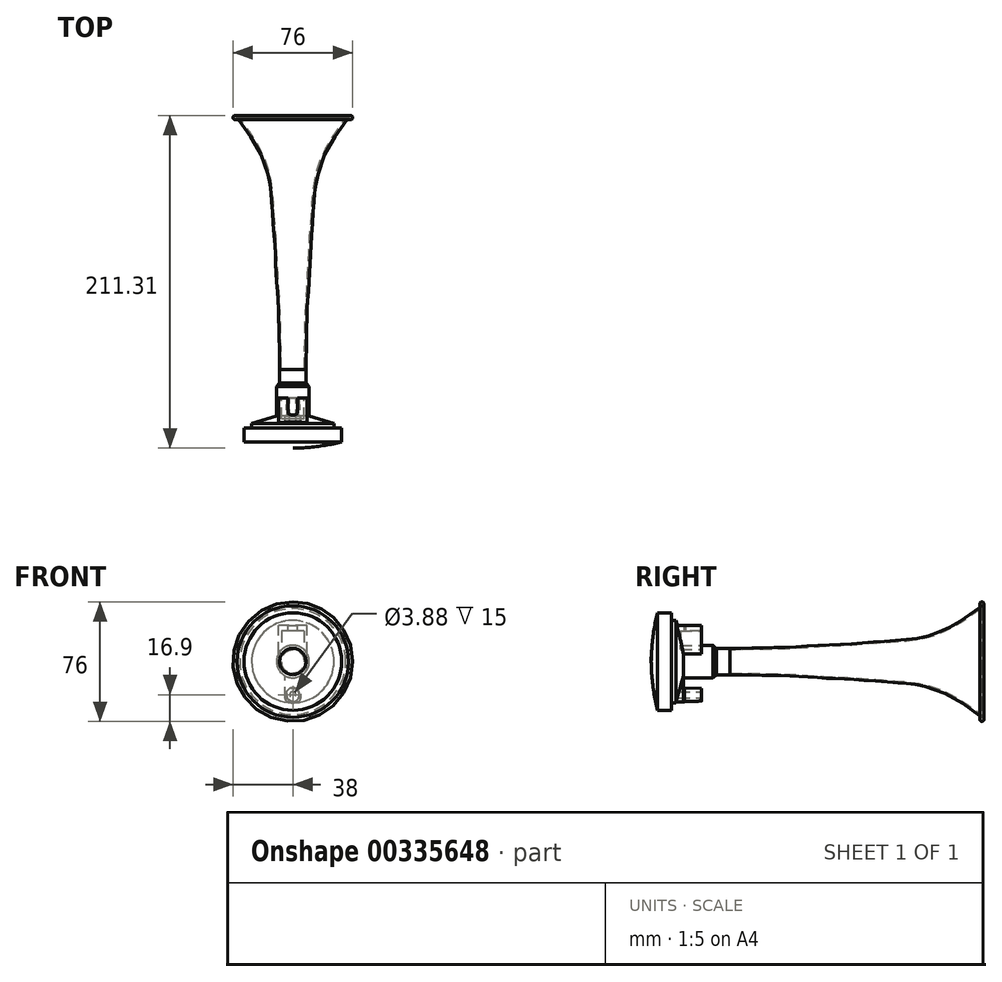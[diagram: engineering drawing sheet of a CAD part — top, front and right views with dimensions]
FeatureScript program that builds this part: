
annotation { "Feature Type Name" : "Feature", "Feature Type Description" : "" }
export const myFeature = defineFeature(function(context is Context, id is Id, definition is map)
    precondition{}
    {
        {
            var Q0;
            Q0=qCreatedBy(makeId("Right.planeOp"),FACE);
            var sketch = newSketch(context, id + "F0", { "sketchPlane" : qUnion([Q0])});
            skLineSegment(sketch, "E0", {"start": v(0, 0) * mm, "end": v(0, 36.7) * mm, "construction": true});
            skLineSegment(sketch, "E1", {"start": v(0, 36.7) * mm, "end": v(0, 36.7) * mm});
            skLineSegment(sketch, "E2", {"start": v(0, 38) * mm, "end": v(0, 36.7) * mm});
            skArc(sketch, "E3", {"start": v(1, 35.86) * mm, "mid": v(-0.55, 37.88) * mm, "end": v(0, 35.4) * mm});
            skPoint(sketch, "E4", {"position": v(1, 35.86) * mm});
            skPoint(sketch, "E5", {"position": v(-20, 0) * mm});
            skPoint(sketch, "E6.1.0.0", {"position": v(-40, 0) * mm});
            skPoint(sketch, "E6.2.0.0", {"position": v(-60, 0) * mm});
            skPoint(sketch, "E6.3.0.0", {"position": v(-80, 0) * mm});
            skPoint(sketch, "E6.4.0.0", {"position": v(-100, 0) * mm});
            skPoint(sketch, "E6.5.0.0", {"position": v(-120, 0) * mm});
            skPoint(sketch, "E6.6.0.0", {"position": v(-140, 0) * mm});
            skPoint(sketch, "E6.7.0.0", {"position": v(-160, 0) * mm});
            skPoint(sketch, "E6.8.0.0", {"position": v(-180, 0) * mm});
            skPoint(sketch, "E6.9.0.0", {"position": v(-200, 0) * mm});
            skPoint(sketch, "E6.10.0.0", {"position": v(-220, 0) * mm});
            skPoint(sketch, "E6.11.0.0", {"position": v(-240, 0) * mm});
            skLineSegment(sketch, "E6.direction1", {"start": v(-20, 0) * mm, "end": v(-40, 0) * mm, "construction": true});
            skLineSegment(sketch, "E7", {"start": v(-20, 0) * mm, "end": v(-20, 22) * mm, "construction": true});
            skLineSegment(sketch, "E8", {"start": v(-40, 0) * mm, "end": v(-40, 15) * mm, "construction": true});
            skLineSegment(sketch, "E9", {"start": v(-60, 0) * mm, "end": v(-60, 13) * mm, "construction": true});
            skLineSegment(sketch, "E10", {"start": v(-80, 0) * mm, "end": v(-80, 11.5) * mm, "construction": true});
            skLineSegment(sketch, "E11", {"start": v(-100, 0) * mm, "end": v(-100, 10.5) * mm, "construction": true});
            skLineSegment(sketch, "E12", {"start": v(-120, 0) * mm, "end": v(-120, 9.25) * mm, "construction": true});
            skLineSegment(sketch, "E13", {"start": v(-140, 0) * mm, "end": v(-140, 8.7) * mm, "construction": true});
            skLineSegment(sketch, "E14", {"start": v(-160, 0) * mm, "end": v(-160, 8.35) * mm, "construction": true});
            skFitSpline(sketch, "E15", {"points": [v(0, 35.4) * mm, v(-20, 22) * mm, v(-40, 15) * mm, v(-60, 13) * mm, v(-80, 11.5) * mm, v(-100, 10.5) * mm, v(-120, 9.25) * mm, v(-140, 8.7) * mm, v(-160, 8.35) * mm], "startDerivative": vector(-145.86, -108.6) * mm, "endDerivative": vector(-162.63, -2.88) * mm});
            skLineSegment(sketch, "E16", {"start": v(-160, 8.35) * mm, "end": v(-168.6, 8.35) * mm});
            skLineSegment(sketch, "E17", {"start": v(-168.6, 8.35) * mm, "end": v(-170.83, 10.35) * mm});
            skLineSegment(sketch, "E18", {"start": v(-170.83, 10.35) * mm, "end": v(-189.63, 10.35) * mm});
            skLineSegment(sketch, "E19", {"start": v(-189.63, 10.35) * mm, "end": v(-194.23, 26.15) * mm});
            skLineSegment(sketch, "E20", {"start": v(-194.23, 26.15) * mm, "end": v(-197.23, 26.15) * mm});
            skLineSegment(sketch, "E21", {"start": v(-197.23, 26.15) * mm, "end": v(-197.23, 31) * mm});
            skLineSegment(sketch, "E22", {"start": v(-197.23, 31) * mm, "end": v(-206, 31) * mm});
            skArc(sketch, "E23", {"start": v(-206, 31) * mm, "mid": v(-208.9, 15.62) * mm, "end": v(-210, 0) * mm});
            skFitSpline(sketch, "E24", {"points": [v(1, 35.86) * mm, v(0, 23.41) * mm, v(0, 0) * mm], "startDerivative": vector(-27.01, -39.8) * mm, "endDerivative": vector(0.68, -43.7) * mm});
            skFitSpline(sketch, "E25.0", {"points": [v(0.6, 34.6) * mm, v(-2.44, 32.34) * mm, v(-7.01, 28.93) * mm, v(-13.23, 24.75) * mm, v(-17.19, 22.36) * mm, v(-20.42, 20.64) * mm, v(-23.68, 19.05) * mm, v(-27.81, 17.32) * mm, v(-32.85, 15.63) * mm, v(-37.08, 14.55) * mm, v(-40.5, 13.88) * mm, v(-43.9, 13.33) * mm, v(-48.16, 12.83) * mm, v(-53.26, 12.43) * mm, v(-57.5, 12.17) * mm, v(-60.88, 11.94) * mm, v(-64.26, 11.69) * mm, v(-70.18, 11.22) * mm, v(-76.95, 10.67) * mm, v(-83.74, 10.27) * mm, v(-88.83, 10.03) * mm, v(-93.9, 9.8) * mm, v(-98.98, 9.57) * mm, v(-104.05, 9.26) * mm, v(-110.81, 8.8) * mm, v(-117.6, 8.34) * mm, v(-124.39, 8.05) * mm, v(-131.18, 7.85) * mm, v(-139.66, 7.7) * mm, v(-149.82, 7.53) * mm, v(-156.6, 7.41) * mm, v(-159.98, 7.35) * mm]});
            skArc(sketch, "E26.filletArc", {"start": v(-0.92, 33.47) * mm, "mid": v(-0.2, 34.13) * mm, "end": v(0.39, 34.91) * mm});
            skLineSegment(sketch, "E27", {"start": v(-159.98, 7.35) * mm, "end": v(-160, 0) * mm});
            skLineSegment(sketch, "E28", {"start": v(-160, 0) * mm, "end": v(-210, 0) * mm});
            skSolve(sketch);
        }
        {
            var Q0;
            {var subQ0=sQuery(id+"F0.wireOp",EDGE,"E15");Q0=makeQuery(id+"F0.imprint","IMPRINT",FACE,{"disambiguationData":[TD([[makeQuery(id+"F0.imprint","IMPRINT",EDGE,{"derivedFrom":subQ0}),1.0]])]});}
            var Q1;
            Q1=sQuery(id+"F0.wireOp",EDGE,"E28");
            revolve(context, id + "F1", {"entities" : qUnion([Q0]), "axis" : qUnion([Q1]), "revolveType" : RevolveType.FULL});
        }
        {
            var Q0;
            Q0=qCreatedBy(makeId("Front.planeOp"),FACE);
            cPlane(context, id + "F2", {"entities" : qUnion([Q0]), "cplaneType" : CPlaneType.OFFSET, "offset" : 178 * mm, "width" : 150 * mm, "height" : 150 * mm});
        }
        {
            var Q0;
            Q0=qCreatedBy(id+"F2.planeOp",FACE);
            var sketch = newSketch(context, id + "F3", { "sketchPlane" : qUnion([Q0])});
            skLineSegment(sketch, "E29", {"start": v(0, 0) * mm, "end": v(0, -25.5) * mm, "construction": true});
            skLineSegment(sketch, "E30", {"start": v(-4.9, -25.5) * mm, "end": v(4.9, -25.5) * mm});
            skPoint(sketch, "E31", {"position": v(0, -25.5) * mm});
            skLineSegment(sketch, "E32", {"start": v(-4.9, -25.5) * mm, "end": v(-4.9, 0) * mm});
            skLineSegment(sketch, "E33", {"start": v(-4.9, 0) * mm, "end": v(4.9, 0) * mm});
            skLineSegment(sketch, "E34", {"start": v(4.9, 0) * mm, "end": v(4.9, -25.5) * mm});
            skSolve(sketch);
        }
        {
            var Q0;
            Q0=makeQuery(id+"F3.imprint","IMPRINT",FACE,{"disambiguationData":[TD([[makeQuery(id+"F3.imprint","IMPRINT",EDGE,{"derivedFrom":sQuery(id+"F3.wireOp",EDGE,"E30")}),1.0]])]});
            extrude(context, id + "F4", {"entities" : qUnion([Q0]), "operationType" : NewBodyOperationType.ADD, "depth" : 25 * mm});
        }
        {
            var Q0;
            Q0=makeQuery(id+"F4.opExtrude","CAP_FACE",FACE,{"disambiguationData":[OSD([sQuery(id+"F3.wireOp",EDGE,"E30"),sQuery(id+"F3.wireOp",EDGE,"E32"),sQuery(id+"F3.wireOp",EDGE,"E33"),sQuery(id+"F3.wireOp",EDGE,"E34")])],"isStart":true});
            extrude(context, id + "F5", {"entities" : qUnion([Q0]), "operationType" : NewBodyOperationType.REMOVE, "oppositeDirection" : true, "depth" : 11.5 * mm});
        }
        {
            var Q0;
            Q0=makeQuery(id+"F4.opExtrude","SWEPT_EDGE",EDGE,{"disambiguationData":[OSD([sQuery(id+"F3.wireOp",EDGE,"E30"),sQuery(id+"F3.wireOp",EDGE,"E32")])]});
            var Q1;
            Q1=makeQuery(id+"F4.opExtrude","SWEPT_EDGE",EDGE,{"disambiguationData":[OSD([sQuery(id+"F3.wireOp",EDGE,"E30"),sQuery(id+"F3.wireOp",EDGE,"E34")])]});
            fillet(context, id + "F6", {"entities" : qUnion([Q0, Q1]), "radius" : 2 * mm, "tangentPropagation" : true, "allowEdgeOverflow" : false});
        }
        {
            var Q0;
            Q0=makeQuery(id+"F5.boolean.opBoolean","COPY",FACE,{"derivedFrom":makeQuery(id+"F5.opExtrude","CAP_FACE",FACE,{"disambiguationData":[OSD([sQuery(id+"F3.wireOp",EDGE,"E30"),sQuery(id+"F3.wireOp",EDGE,"E32"),sQuery(id+"F3.wireOp",EDGE,"E33"),sQuery(id+"F3.wireOp",EDGE,"E34")])],"isStart":false})});
            var sketch = newSketch(context, id + "F7", { "sketchPlane" : qUnion([Q0])});
            skLineSegment(sketch, "E35", {"start": v(0, -25.5) * mm, "end": v(0, -21.1) * mm, "construction": true});
            skPoint(sketch, "E35.endSnap0", {"position": v(0, -25.5) * mm});
            skCircle(sketch, "E36", {"center": v(0, -21.1) * mm, "radius": 4.4 * mm});
            skSolve(sketch);
        }
        {
            var Q0;
            Q0=qCreatedBy(id+"F2.planeOp",FACE);
            var sketch = newSketch(context, id + "F8", { "sketchPlane" : qUnion([Q0])});
            skPoint(sketch, "E37", {"position": v(0, -21.1) * mm});
            skCircle(sketch, "E38", {"center": v(0, -21.1) * mm, "radius": 4 * mm});
            skSolve(sketch);
        }
        {
            var Q0;
            Q0=makeQuery(id+"F7.imprint","IMPRINT",FACE,{"disambiguationData":[TD([[makeQuery(id+"F7.imprint","IMPRINT",EDGE,{"derivedFrom":sQuery(id+"F7.wireOp",EDGE,"E36")}),1.0]])]});
            var Q1;
            Q1=sQuery(id+"F7.wireOp",EDGE,"E36");
            extrude(context, id + "F9", {"entities" : qUnion([Q0]), "operationType" : NewBodyOperationType.ADD, "surfaceEntities" : qUnion([Q1]), "depth" : .5 * mm});
        }
        {
            var Q0;
            Q0=makeQuery(id+"F8.imprint","IMPRINT",FACE,{"disambiguationData":[TD([[makeQuery(id+"F8.imprint","IMPRINT",EDGE,{"derivedFrom":sQuery(id+"F8.wireOp",EDGE,"E38")}),1.0]])]});
            extrude(context, id + "F10", {"entities" : qUnion([Q0]), "depth" : .1 * mm});
        }
        {
            var Q1;
            Q1=makeQuery(id+"F10.opExtrude","CAP_FACE",FACE,{"disambiguationData":[OSD([sQuery(id+"F8.wireOp",EDGE,"E38")])],"isStart":false});
            var Q2;
            Q2=makeQuery(id+"F9.opExtrude","CAP_FACE",FACE,{"disambiguationData":[OSD([sQuery(id+"F7.wireOp",EDGE,"E36")])],"isStart":false});
            loft(context, id + "F11", {"operationType" : NewBodyOperationType.ADD, "sheetProfilesArray" : [{ "sheetProfileEntities" : qUnion([Q1]) }, { "sheetProfileEntities" : qUnion([Q2]) }]});
        }
        {
            var Q0;
            Q0=makeQuery(id+"F10.opExtrude","CAP_FACE",FACE,{"disambiguationData":[OSD([sQuery(id+"F8.wireOp",EDGE,"E38")])],"isStart":true});
            var sketch = newSketch(context, id + "F12", { "sketchPlane" : qUnion([Q0])});
            skCircle(sketch, "E39.0", {"center": v(0, -21.1) * mm, "radius": 4 * mm});
            skCircle(sketch, "E40", {"center": v(0, -21.1) * mm, "radius": 1.94 * mm});
            skSolve(sketch);
        }
        {
            var Q0;
            Q0=makeQuery(id+"F12.imprint","IMPRINT",FACE,{"disambiguationData":[TD([[makeQuery(id+"F12.imprint","IMPRINT",EDGE,{"derivedFrom":sQuery(id+"F12.wireOp",EDGE,"E40")}),1.0]])]});
            extrude(context, id + "F13", {"entities" : qUnion([Q0]), "operationType" : NewBodyOperationType.REMOVE, "oppositeDirection" : true, "depth" : 15 * mm});
        }
        {
            var Q0;
            Q0=qCreatedBy(id+"F2.planeOp",FACE);
            var sketch = newSketch(context, id + "F14", { "sketchPlane" : qUnion([Q0])});
            skLineSegment(sketch, "E41.bottom", {"start": v(9.07, 2.58) * mm, "end": v(-9.07, 2.58) * mm});
            skLineSegment(sketch, "E41.top", {"start": v(9.07, 23) * mm, "end": v(-9.07, 23) * mm});
            skLineSegment(sketch, "E41.left", {"start": v(9.07, 2.58) * mm, "end": v(9.07, 23) * mm});
            skLineSegment(sketch, "E41.right", {"start": v(-9.07, 2.58) * mm, "end": v(-9.07, 23) * mm});
            skPoint(sketch, "E42", {"position": v(0, 23) * mm});
            skCircle(sketch, "E43.0", {"center": v(0, 0) * mm, "radius": 31 * mm});
            skSolve(sketch);
        }
        {
            var Q0;
            Q0=makeQuery(id+"F14.imprint","IMPRINT",FACE,{"disambiguationData":[TD([[makeQuery(id+"F14.imprint","IMPRINT",EDGE,{"derivedFrom":sQuery(id+"F14.wireOp",EDGE,"E41.bottom")}),-1.0]])]});
            extrude(context, id + "F15", {"entities" : qUnion([Q0]), "operationType" : NewBodyOperationType.ADD, "depth" : 18 * mm});
        }
        {
            var Q0;
            Q0=makeQuery(id+"F15.opExtrude","CAP_FACE",FACE,{"disambiguationData":[OSD([sQuery(id+"F14.wireOp",EDGE,"E41.bottom"),sQuery(id+"F14.wireOp",EDGE,"E41.top"),sQuery(id+"F14.wireOp",EDGE,"E41.left"),sQuery(id+"F14.wireOp",EDGE,"E41.right")])],"isStart":true});
            var sketch = newSketch(context, id + "F16", { "sketchPlane" : qUnion([Q0])});
            skLineSegment(sketch, "E44", {"start": v(-7.07, 19.5) * mm, "end": v(7.07, 19.5) * mm});
            skLineSegment(sketch, "E45", {"start": v(-7.07, 19.5) * mm, "end": v(-7.07, -7.56) * mm});
            skLineSegment(sketch, "E46", {"start": v(7.07, 19.5) * mm, "end": v(7.07, -7.56) * mm});
            skArc(sketch, "E47.0", {"start": v(-9.07, 4.99) * mm, "mid": v(0, -10.35) * mm, "end": v(9.07, 4.99) * mm});
            skPoint(sketch, "E48.orphan", {"position": v(-7.07, 4.99) * mm});
            skPoint(sketch, "E49.orphan", {"position": v(7.07, 4.99) * mm});
            skSolve(sketch);
        }
        {
            var Q0;
            Q0=makeQuery(id+"F16.imprint","IMPRINT",FACE,{"disambiguationData":[TD([[makeQuery(id+"F16.imprint","IMPRINT",EDGE,{"derivedFrom":sQuery(id+"F16.wireOp",EDGE,"E44")}),-1.0]])]});
            var Q1;
            Q1=makeQuery(id+"F1.opRevolve","SWEPT_FACE",FACE,{"disambiguationData":[OSD([sQuery(id+"F0.wireOp",EDGE,"E19")])]});
            extrude(context, id + "F17", {"entities" : qUnion([Q0]), "operationType" : NewBodyOperationType.REMOVE, "oppositeDirection" : true, "endBoundEntityFace" : qUnion([Q1]), "depth" : 13.5 * mm});
        }
        {
            var Q0;
            Q0=makeQuery(id+"F15.opExtrude","SWEPT_FACE",FACE,{"disambiguationData":[OSD([sQuery(id+"F14.wireOp",EDGE,"E41.top")])]});
            var sketch = newSketch(context, id + "F18", { "sketchPlane" : qUnion([Q0])});
            skLineSegment(sketch, "E50", {"start": v(-3, -178) * mm, "end": v(3, -178) * mm});
            skLineSegment(sketch, "E51", {"start": v(3, -178) * mm, "end": v(3, -187.88) * mm});
            skLineSegment(sketch, "E52", {"start": v(-3, -178) * mm, "end": v(-3, -187.88) * mm});
            skArc(sketch, "E53", {"start": v(-3, -187.88) * mm, "mid": v(0, -189) * mm, "end": v(3, -187.88) * mm});
            skPoint(sketch, "E54", {"position": v(0, -178) * mm});
            skSolve(sketch);
        }
        {
            var Q0;
            Q0=makeQuery(id+"F18.imprint","IMPRINT",FACE,{"disambiguationData":[TD([[makeQuery(id+"F18.imprint","IMPRINT",EDGE,{"derivedFrom":sQuery(id+"F18.wireOp",EDGE,"E50")}),1.0]])]});
            extrude(context, id + "F19", {"entities" : qUnion([Q0]), "operationType" : NewBodyOperationType.REMOVE, "endBound" : BoundingType.UP_TO_NEXT, "oppositeDirection" : true, "depth" : 25 * mm});
        }
    });
